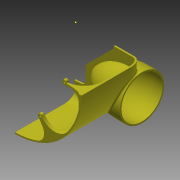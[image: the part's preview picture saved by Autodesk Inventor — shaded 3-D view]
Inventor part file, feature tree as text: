
AUTODESK INVENTOR PART (.ipt)
format: ipt  version: 2015 (Build 190159000, 159)  size: 1,082,880 bytes
history: native  units: mm
features: sketch x19, extrude x16, fillet x9, revolve x5, mirror x1
ambient origin geometry x8: Origin, YZ Plane, XZ Plane, XY Plane, X Axis, Y Axis, Z Axis, Center Point
bodies: Body1 (feature_tree)
feature tree (50):
  sketch  "Boceto1"  dims[d1=40.0mm d2=20.0mm d3=20.0mm d4=5.0mm d5=360.0deg d6=5.0mm d7=5.0mm d9=5.0mm d10=10.0mm d11=2.451216mm d13=270.0mm]
  revolve  "Revolución1"  [1 undecoded]
  sketch  "Boceto3"  dims[d20=3.0mm d21=120.0mm]
  extrude  "Extrusión2"  Depth=100.0mm
  extrude  "Extrusión3"  Depth=120.0mm
  sketch  "Boceto6"  dims[d22=3.0mm d23=120.0mm]
  revolve  "Revolución2"  [1 undecoded]
  revolve  "Revolución3"  [1 undecoded]
  revolve  "Revolución4"  [1 undecoded]
  revolve  "Revolución5"  [1 undecoded]
  fillet  "Empalme2"  Radius=100.0mm
  sketch  "Boceto7"  dims[d24=90.0deg]
  extrude  "Extrusión7"  Depth=20.0mm
  extrude  "Extrusión8"  Depth=3.0mm
  extrude  "Extrusión9"  TaperAngle=90.0deg  [1 undecoded]
  extrude  "Extrusión10"  TaperAngle=90.0deg  [1 undecoded]
  fillet  "Empalme4"  Radius=3.0mm
  fillet  "Empalme5"  Radius=20.0mm
  sketch  "Boceto16"  dims[d57=135.0mm d58=3.0mm]
  extrude  "Extrusión11"  Depth=10.0mm
  extrude  "Extrusión12"  Depth=10.0mm TaperAngle=0.0deg
  fillet  "Empalme6"  Radius=8.0mm
  extrude  "Extrusión13"  Depth=8.0mm
  fillet  "Empalme7"  Radius=8.0mm
  mirror  "Simetría1"
  sketch  "Boceto20"  dims[d73=10.0mm d74=111.0mm d75=0.0mm d79=8.0mm]
  extrude  "Extrusión14"  Depth=20.0mm TaperAngle=360.0deg
  extrude  "Extrusión15"  Depth=6.0mm TaperAngle=0.0deg
  extrude  "Extrusión16"  Depth=20.0mm
  extrude  "Extrusión17"  Depth=1.0mm TaperAngle=0.0deg
  extrude  "Extrusión18"  Depth=1.0mm TaperAngle=0.0deg
  extrude  "Extrusión19"  Depth=1.0mm
  fillet  "Empalme12"  Radius=6.0mm
  fillet  "Empalme13"  Radius=2.0mm
  fillet  "Empalme14"  Radius=6.0mm
  fillet  "Empalme15"  Radius=6.0mm
  extrude  "Extrusión20"  Depth=1.0mm TaperAngle=0.0deg
  sketch  "Boceto2"  dims[d14=3.0mm d19=100.0mm]
  sketch  "Boceto11"  dims[d26=40.0mm d27=20.0mm d28=20.0mm d29=5.0mm d30=360.0deg d31=5.0mm d32=5.0mm d33=5.0mm d34=10.0mm d35=2.451216mm d36=270.0mm d37=3.0mm d38=60.0mm d39=0.0mm]
  sketch  "Boceto12"  dims[d40=3.0mm d41=0.0mm d51=20.0mm]
  sketch  "Boceto13"  dims[d52=45.0mm d53=20.0mm d54=100.0mm]
  sketch  "Boceto14"  dims[d55=90.0deg d56=20.0mm]
  sketch  "Boceto17"  dims[d59=90.0deg d60=90.0deg]
  sketch  "Boceto18"  dims[d61=90.0deg d62=90.0deg d63=3.0mm d69=20.0mm]
  sketch  "Boceto19"  dims[d70=10.0mm d71=10.0mm]
  sketch  "Boceto21"  dims[d80=8.0mm d81=8.0mm d82=8.0mm]
  sketch  "Boceto22"  dims[d83=6.0mm d84=0.0mm d87=20.0mm d89=360.0deg]
  sketch  "Boceto23"  dims[d91=6.0mm d92=0.0mm d93=6.0mm d94=0.0mm]
  sketch  "Boceto24"  dims[d95=30.0mm d96=20.0mm]
  sketch  "Boceto25"  dims[d97=60.0deg d98=1111.0mm d99=0.0mm d100=6.0mm d101=0.0mm d102=1.0mm d103=6.0mm d104=0.0mm d105=2.0mm d106=6.0mm d107=0.0mm d108=6.0mm d109=0.0mm d110=6.0mm d111=0.0mm d113=3.0mm d114=0.0mm d115=3.0mm d116=0.0mm d117=6.0mm d118=0.0mm d123=40.0mm d124=10.0mm d125=1.0mm d126=1.0mm d128=20.0mm d129=0.0mm]
note: 7 required parameter values undecoded (feature->parameter linkage not recoverable at this tier; creation-order binding heuristic only, values carry confidence <= 0.55)